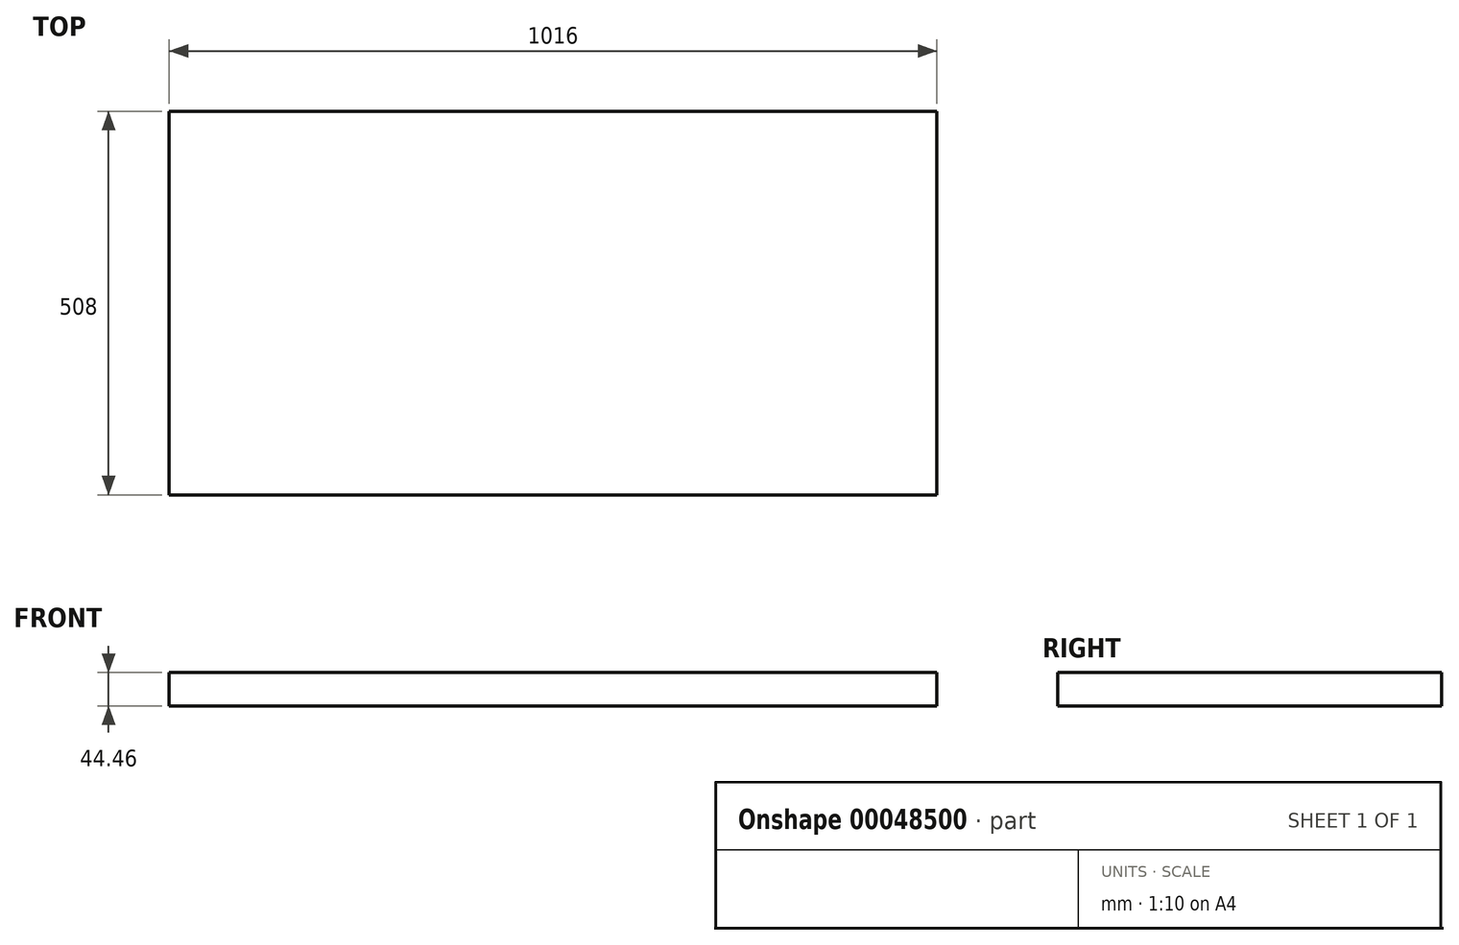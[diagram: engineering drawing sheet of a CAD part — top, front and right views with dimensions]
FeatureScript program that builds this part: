
annotation { "Feature Type Name" : "Feature", "Feature Type Description" : "" }
export const myFeature = defineFeature(function(context is Context, id is Id, definition is map)
    precondition{}
    {
        {
            var Q0;
            Q0=qCreatedBy(makeId("Front.planeOp"),FACE);
            var sketch = newSketch(context, id + "F0", { "sketchPlane" : qUnion([Q0])});
            skLineSegment(sketch, "E0.bottom", {"start": v(-508, 22.23) * mm, "end": v(508, 22.23) * mm});
            skLineSegment(sketch, "E0.top", {"start": v(-508, -22.22) * mm, "end": v(508, -22.22) * mm});
            skLineSegment(sketch, "E0.left", {"start": v(-508, 22.23) * mm, "end": v(-508, -22.22) * mm});
            skLineSegment(sketch, "E0.right", {"start": v(508, 22.23) * mm, "end": v(508, -22.22) * mm});
            skSolve(sketch);
        }
        {
            var Q0;
            Q0=makeQuery(id+"F0.imprint","IMPRINT",FACE,{"disambiguationData":[TD([[makeQuery(id+"F0.imprint","IMPRINT",EDGE,{"derivedFrom":sQuery(id+"F0.wireOp",EDGE,"E0.bottom")}),-1.0]])]});
            extrude(context, id + "F1", {"entities" : qUnion([Q0]), "depth" : 508 * mm});
        }
    });
